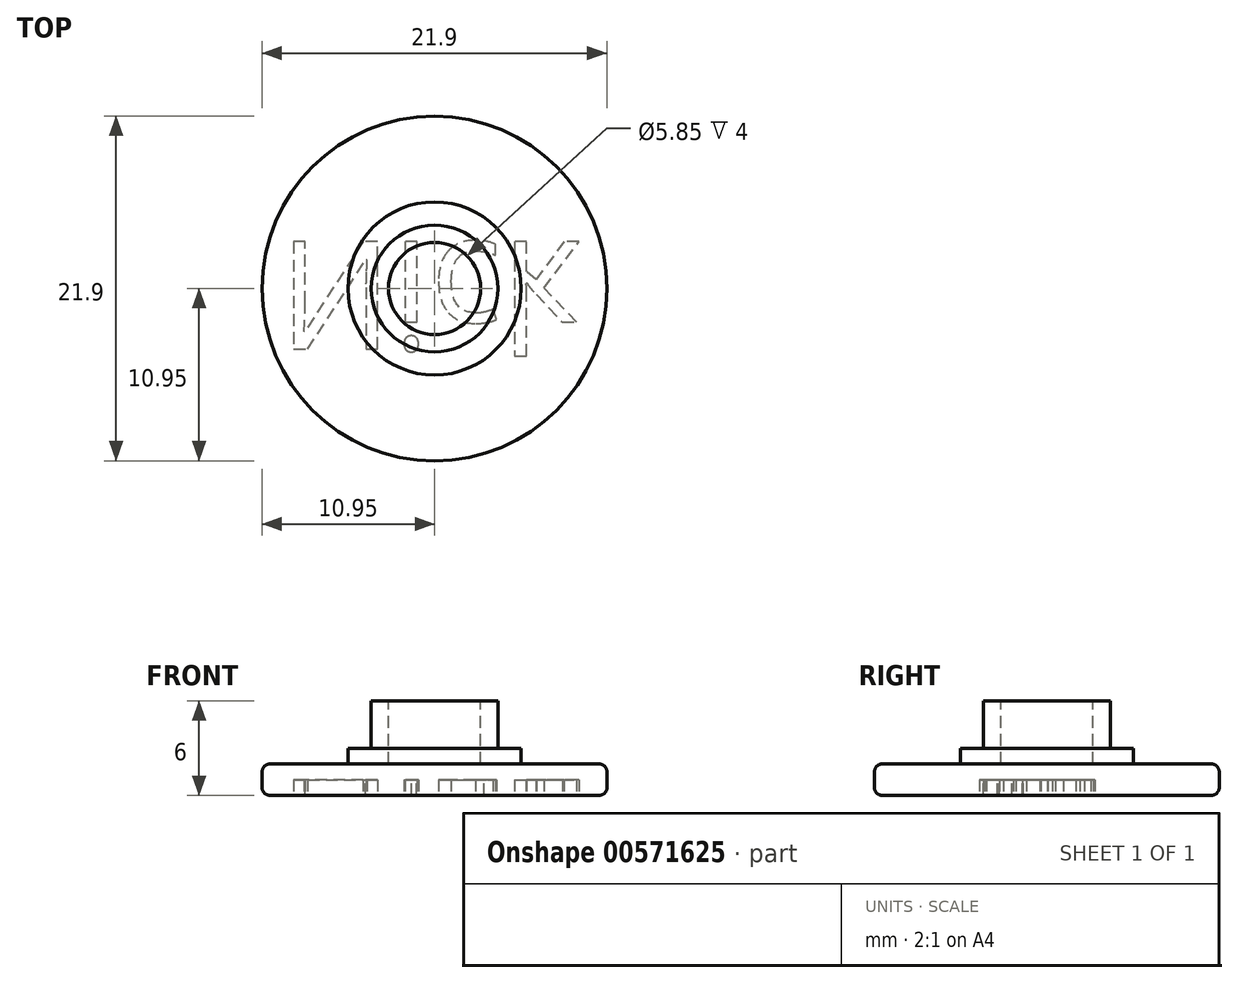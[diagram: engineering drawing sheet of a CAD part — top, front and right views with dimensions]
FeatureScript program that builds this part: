
annotation { "Feature Type Name" : "Feature", "Feature Type Description" : "" }
export const myFeature = defineFeature(function(context is Context, id is Id, definition is map)
    precondition{}
    {
        {
            var Q0;
            Q0=qCreatedBy(makeId("Top.planeOp"),FACE);
            var sketch = newSketch(context, id + "F0", { "sketchPlane" : qUnion([Q0])});
            skCircle(sketch, "E0", {"center": v(0, 0) * mm, "radius": 0.07 * mm});
            skCircle(sketch, "E1", {"center": v(0, 0) * mm, "radius": 10.95 * mm});
            skSolve(sketch);
        }
        {
            var Q0;
            Q0=qCreatedBy(makeId("Top.planeOp"),FACE);
            var sketch = newSketch(context, id + "F1", { "sketchPlane" : qUnion([Q0])});
            skCircle(sketch, "E2", {"center": v(0, 0) * mm, "radius": 5.5 * mm});
            skSolve(sketch);
        }
        {
            var Q0;
            Q0=qCreatedBy(makeId("Top.planeOp"),FACE);
            var sketch = newSketch(context, id + "F2", { "sketchPlane" : qUnion([Q0])});
            skCircle(sketch, "E3", {"center": v(0, 0) * mm, "radius": 4.03 * mm});
            skSolve(sketch);
        }
        {
            var Q0;
            Q0=qSketchRegion(id+"F0",true);
            extrude(context, id + "F3", {"entities" : qUnion([Q0]), "depth" : 2 * mm});
        }
        {
            var Q0;
            Q0=qSketchRegion(id+"F1",true);
            extrude(context, id + "F4", {"entities" : qUnion([Q0]), "operationType" : NewBodyOperationType.ADD, "depth" : 3 * mm});
        }
        {
            var Q0;
            Q0=qSketchRegion(id+"F2",true);
            extrude(context, id + "F5", {"entities" : qUnion([Q0]), "operationType" : NewBodyOperationType.ADD, "depth" : 6 * mm});
        }
        {
            var Q0;
            Q0=makeQuery(id+"F3.opExtrude","SWEPT_FACE",FACE,{"disambiguationData":[OSD([sQuery(id+"F0.wireOp",EDGE,"E1")])]});
            fillet(context, id + "F6", {"entities" : qUnion([Q0]), "radius" : .5 * mm, "tangentPropagation" : true, "allowEdgeOverflow" : false});
        }
        {
            var Q0;
            Q0=makeQuery(id+"F5.opExtrude","CAP_FACE",FACE,{"disambiguationData":[OSD([sQuery(id+"F2.wireOp",EDGE,"E3")])],"isStart":false});
            var sketch = newSketch(context, id + "F7", { "sketchPlane" : qUnion([Q0])});
            skCircle(sketch, "E4.0", {"center": v(0, 0) * mm, "radius": 2.92 * mm});
            skSolve(sketch);
        }
        {
            var Q0;
            Q0=qSketchRegion(id+"F7",true);
            extrude(context, id + "F8", {"entities" : qUnion([Q0]), "operationType" : NewBodyOperationType.REMOVE, "oppositeDirection" : true, "depth" : 4 * mm});
        }
        {
            var Q0;
            Q0=makeQuery(id+"F4.boolean.opBoolean","MERGE",FACE,{"derivedFrom":[makeQuery(id+"F3.opExtrude","CAP_FACE",FACE,{"disambiguationData":[OSD([sQuery(id+"F0.wireOp",EDGE,"E0"),sQuery(id+"F0.wireOp",EDGE,"E1")])],"isStart":true}),makeQuery(id+"F4.opExtrude","CAP_FACE",FACE,{"disambiguationData":[OSD([sQuery(id+"F1.wireOp",EDGE,"E2")])],"isStart":true})]});
            var sketch = newSketch(context, id + "F9", { "sketchPlane" : qUnion([Q0])});
            skText(sketch, "E5", { "text": "Nick\n", "fontName": "OpenSans-Regular.ttf"});
            const initialGuessF9  = {"E5": [-0.00988, -0.00297, 1, 0, 0.00687]};
            skSetInitialGuess(sketch, initialGuessF9);
            skSolve(sketch);
        }
        {
            var Q0;
            Q0 = qSketchRegion(id + "F9", true);
            extrude(context, id + "F10", {"entities" : qUnion([Q0]), "operationType" : NewBodyOperationType.REMOVE, "oppositeDirection" : true, "depth" : 1 * mm, "offsetDistance" : 25 * mm});
        }
    });
